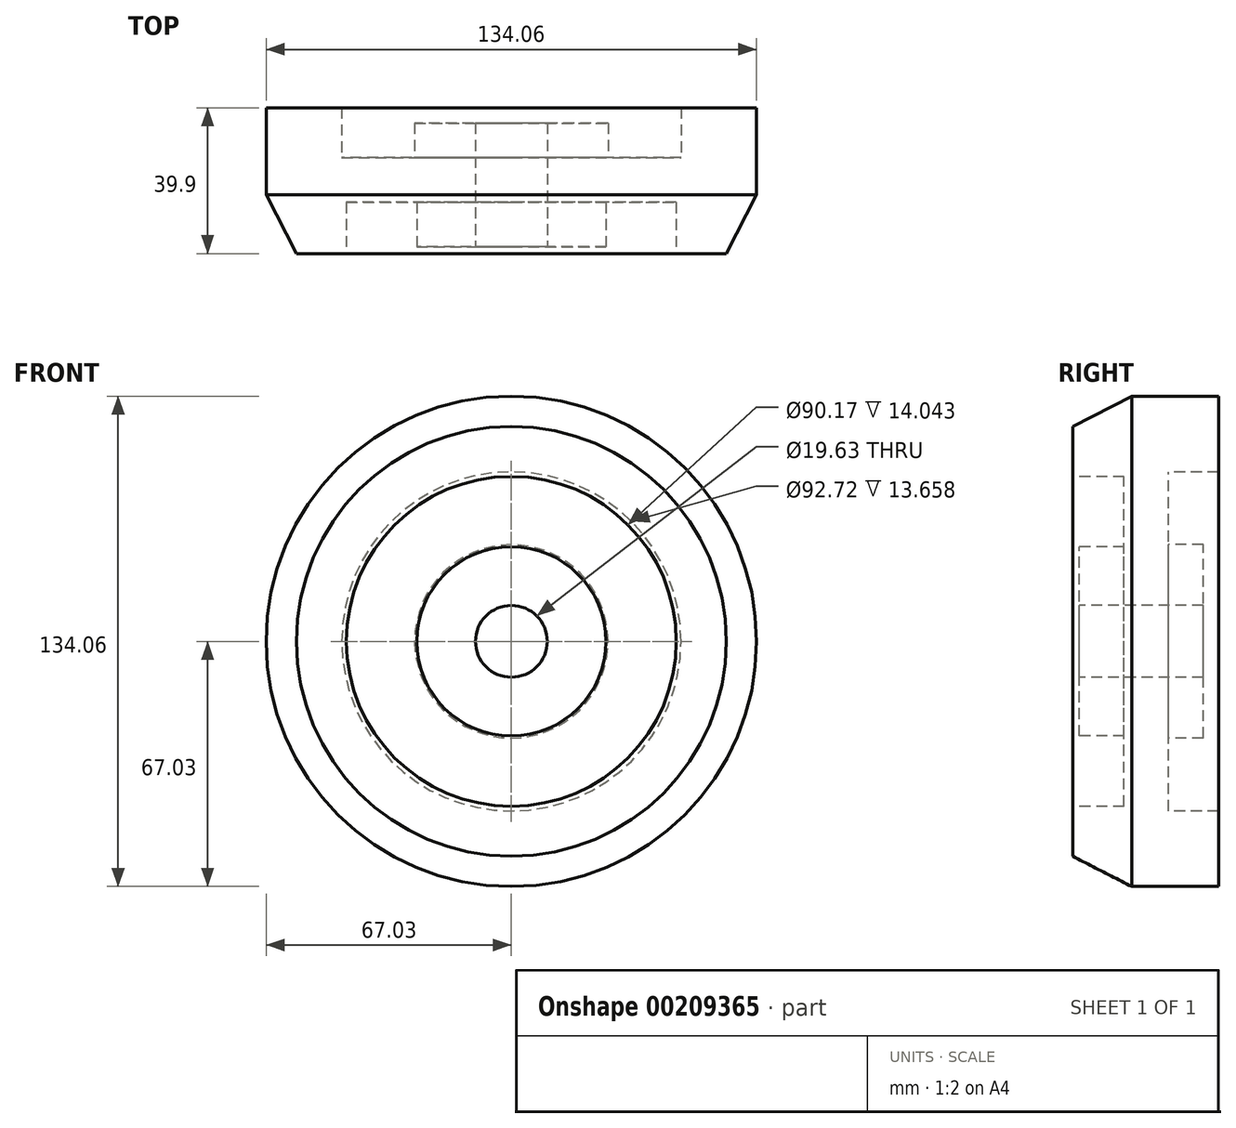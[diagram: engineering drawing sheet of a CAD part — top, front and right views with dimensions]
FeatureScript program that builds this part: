
annotation { "Feature Type Name" : "Feature", "Feature Type Description" : "" }
export const myFeature = defineFeature(function(context is Context, id is Id, definition is map)
    precondition{}
    {
        {
            var Q0;
            Q0=qCreatedBy(makeId("Right.planeOp"),FACE);
            var sketch = newSketch(context, id + "F0", { "sketchPlane" : qUnion([Q0])});
            skLineSegment(sketch, "E0", {"start": v(0, 74.28) * mm, "end": v(0, 0) * mm});
            skLineSegment(sketch, "E1", {"start": v(0, 0) * mm, "end": v(72.43, 0) * mm});
            skLineSegment(sketch, "E2", {"start": v(18.85, 58.76) * mm, "end": v(18.85, 45.09) * mm});
            skLineSegment(sketch, "E3", {"start": v(18.85, 45.09) * mm, "end": v(32.9, 45.09) * mm});
            skLineSegment(sketch, "E4", {"start": v(32.9, 45.09) * mm, "end": v(32.9, 25.87) * mm});
            skLineSegment(sketch, "E5", {"start": v(32.9, 25.87) * mm, "end": v(20.7, 25.87) * mm});
            skLineSegment(sketch, "E6", {"start": v(20.7, 25.87) * mm, "end": v(20.7, 9.82) * mm});
            skLineSegment(sketch, "E7", {"start": v(20.7, 9.82) * mm, "end": v(54.5, 9.82) * mm});
            skLineSegment(sketch, "E8", {"start": v(54.5, 9.82) * mm, "end": v(54.5, 26.43) * mm});
            skLineSegment(sketch, "E9", {"start": v(54.5, 26.43) * mm, "end": v(45.1, 26.43) * mm});
            skLineSegment(sketch, "E10", {"start": v(45.1, 26.43) * mm, "end": v(45.1, 46.36) * mm});
            skLineSegment(sketch, "E11", {"start": v(45.1, 46.36) * mm, "end": v(58.75, 46.36) * mm});
            skLineSegment(sketch, "E12", {"start": v(58.75, 46.36) * mm, "end": v(58.75, 67.03) * mm});
            skLineSegment(sketch, "E13", {"start": v(58.75, 67.03) * mm, "end": v(34.94, 67.03) * mm});
            skLineSegment(sketch, "E14", {"start": v(34.94, 67.03) * mm, "end": v(18.85, 58.76) * mm});
            skSolve(sketch);
        }
        {
            var Q0;
            Q0=makeQuery(id+"F0.imprint","IMPRINT",FACE,{"disambiguationData":[TD([[makeQuery(id+"F0.imprint","IMPRINT",EDGE,{"derivedFrom":sQuery(id+"F0.wireOp",EDGE,"E2")}),1.0]])]});
            var Q1;
            Q1=sQuery(id+"F0.wireOp",EDGE,"E1");
            revolve(context, id + "F1", {"entities" : qUnion([Q0]), "axis" : qUnion([Q1]), "revolveType" : RevolveType.FULL});
        }
        {
            var Q0;
            Q0=qCreatedBy(makeId("Front.planeOp"),FACE);
            var sketch = newSketch(context, id + "F2", { "sketchPlane" : qUnion([Q0])});
            skCircle(sketch, "E15", {"center": v(22.32, -66.37) * mm, "radius": 6.95 * mm});
            skSolve(sketch);
        }
        {
            var Q0;
            Q0=sQuery(id+"F2.wireOp",EDGE,"E15");
            extrude(context, id + "F3", {"bodyType" : ToolBodyType.SURFACE, "surfaceEntities" : qUnion([Q0]), "oppositeDirection" : true, "depth" : 0.23 * yard});
        }
    });
